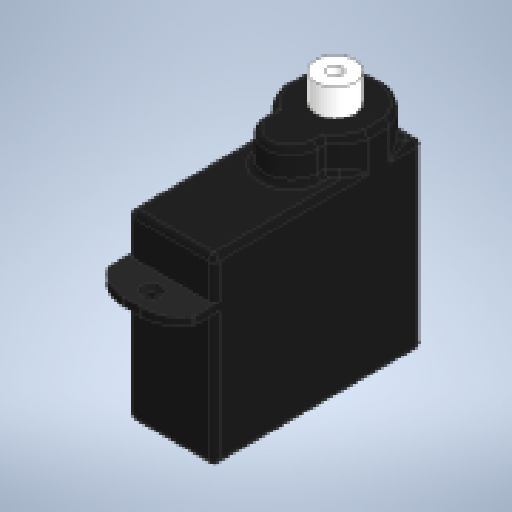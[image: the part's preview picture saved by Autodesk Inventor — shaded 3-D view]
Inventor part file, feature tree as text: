
AUTODESK INVENTOR PART (.ipt)
format: ipt  version: 2023 (Build 270158000, 158)  size: 954,880 bytes
history: native  units: in
note: dims shown in document units (in); Inventor stores cm internally (conversion verified against a paired STEP export)
features: extrude x8, projected_geometry x7, sketch x6, fillet x4
ambient origin geometry x8: Origin, YZ Plane, XZ Plane, XY Plane, X Axis, Y Axis, Z Axis, Center Point
bodies: Solid1 (feature_tree)
feature tree (25):
  extrude  "Extrusion1"  Depth=0.7874in
  extrude  "Extrusion2"  Depth=0.3346in
  extrude  "Extrusion3"  Depth=0.1181in TaperAngle=0.0deg
  sketch  "Sketch4"  dims[d9=0.1496in d10=0.0512in]
  extrude  "Extrusion4"  Depth=0.0512in
  extrude  "Extrusion5"  Depth=0.0197in TaperAngle=0.0deg
  fillet  "Fillet1"  Radius=0.1457in
  fillet  "Fillet2"  Radius=0.126in
  fillet  "Fillet3"  Radius=0.126in
  sketch  "Sketch5"  dims[d12=53.1496in d14=360.0deg d16=0.1024in d17=0.0in d18=0.1457in d19=0.126in d20=0.126in d21=0.1831in d22=0.0in d23=0.1516in d24=0.0in d25=0.0197in d26=0.0197in d27=0.0197in d28=0.1516in d29=0.0in d30=0.3937in d31=0.0in d32=0.0197in d33=0.0in d34=0.0in]
  extrude  "Extrusion6"  Depth=0.0197in TaperAngle=0.0deg
  extrude  "Extrusion7"  Depth=0.0197in TaperAngle=0.0deg
  fillet  "Fillet4"  Radius=0.0197in
  extrude  "Wyciągnięcie proste8"  Depth=0.0197in
  sketch  "Sketch1"  dims[d0=0.3248in d1=0.7874in]
  sketch  "Sketch2"  dims[d2=0.689in d3=0.0in d5=0.3346in]
  projected_geometry  "Projected Loop1"
  sketch  "Sketch3"  dims[d6=0.1969in d7=0.1181in d8=0.0in]
  projected_geometry  "Projected Loop2"
  projected_geometry  "Projected Loop3"
  projected_geometry  "Projected Loop4"
  projected_geometry  "Projected Loop5"
  projected_geometry  "Projected Loop6"
  sketch  "Szkic6"
  projected_geometry  "Pętla rzutowana7"
